# Revit family: NBS_CMDLtd_PwrBsbrTrnkng_BetatrakUnderfloorBusbar_1200mm
name_source: partatom
category: Electrical Fixtures
revit_build: Autodesk Revit 2016 (Build: 20150220_1215(x64)
units: mm (PartAtom-declared; Revit-internal decimal feet)

## family parameters
Cut with Voids When Loaded = No
Host = Face
Maintain Annotation Orientation = No
Part Type = Normal
Room Calculation Point = No
Round Connector Dimension = Use Diameter
Shared = No

## types (1)
- Standard
    AccessoryOptions = Feed units; tap-off units; flexible corners and kits
    Assembly = Fully type-tested
    AssetType = Fixed
    AttitudeOptions = Horizontal; Vertical
    BIMObjectName = NBS_CMDLtd_PowerBusbarTrunking_BetatrakUnderfloorBusbar_1200mm-Standard
    BusbarHeight = 19 mm
    BusbarLength = 1252 mm  [stored 4.10761 ft]
    BusbarMaterial = NBS_Concept
    BusbarWidth = 76 mm  [stored 0.249344 ft]
    CableInsulationMaterial = Flame Retardant Polycarbonate
    CasingColour = Steel, metallic
    CasingFinish = Self finished
    CasingMaterial = Galvanized steel
    Category = Pr_60_70_48_07:Busbar trunking feed units
    CentreOffset = 0 mm  [stored 0 ft]
    Conductors = Copper
    CrossSectionalArea = 0 m²
    CurrentRating = 63 A
    Default Elevation = 0 mm  [stored 0 ft]
    Description = Click-fit underfloor power distribution
    DurationUnit = year
    Features = Choice: a comprehensive range of supply systems. Flexibility: can be used in new or existing layouts. Versatility: all kinds of configurations are possible including bends/corners. Safety: colour coded tap offs for easy recognition. Sliding dust covers to protect outlets. Height clearance: low profile busbar suitable for shallow floor voids. Convenience: variety of Betatrak® lengths with different socket centres. 300 mm standard (150 mm and 600 mm available on request)
    Finish = Galvanized steel
    IfcExportAs = IfcCableSegmentType
    IfcExportType = CABLESEGMENT
    ManufacturerName = CMD Ltd
    ManufacturerURL = www.cmd-ltd.com
    MaxOperatingTemperature = 0
    ModelNumber = PBST3312
    ModelReference = Betatrak Underfloor Busbar
    NBSCertification = www.nationalbimlibrary.com/cert/m0qxcgie
    NBSDescription = Power busbar trunking
    NBSReference = 90-50-45/320
    Name = PowerBusbarTrunking_BetatrakUnderfloorBusbar_1200mm-Standard_CMDLtd
    NominalHeight = 75 mm
    NominalLength = 1200 mm
    NominalWidth = 38 mm
    NominalWidthOrDiameter = 38 mm
    NormalOperatingTemperature = 0
    NumberOfSockets = 4
    PlaceOfInstallationOptions = Indoor; Underfloor
    ProductInformation = www.cmd-ltd.com/products/betatrak-busbar
    Size = 1200 x 38 x 75 mm
    SocketDistance = 300 mm
    SocketNumber = 4
    SocketOffsetFromEnd = 200 mm  [stored 0.656168 ft]
    Uniclass2015Code = Pr_60_70_48_07
    Uniclass2015Title = Busbar trunking feed units
    Uniclass2015Version = Products v1.3
    Version = 2
    VoltageRating = High voltage
    WarrantyDurationUnit = year

note: [stored X ft] marks values corroborated as IEEE doubles in the binary element streams (Revit-internal decimal feet)

## geometry (parser evidence)
native form markers: Sweep x5
no freeform markers — native parametric forms only
